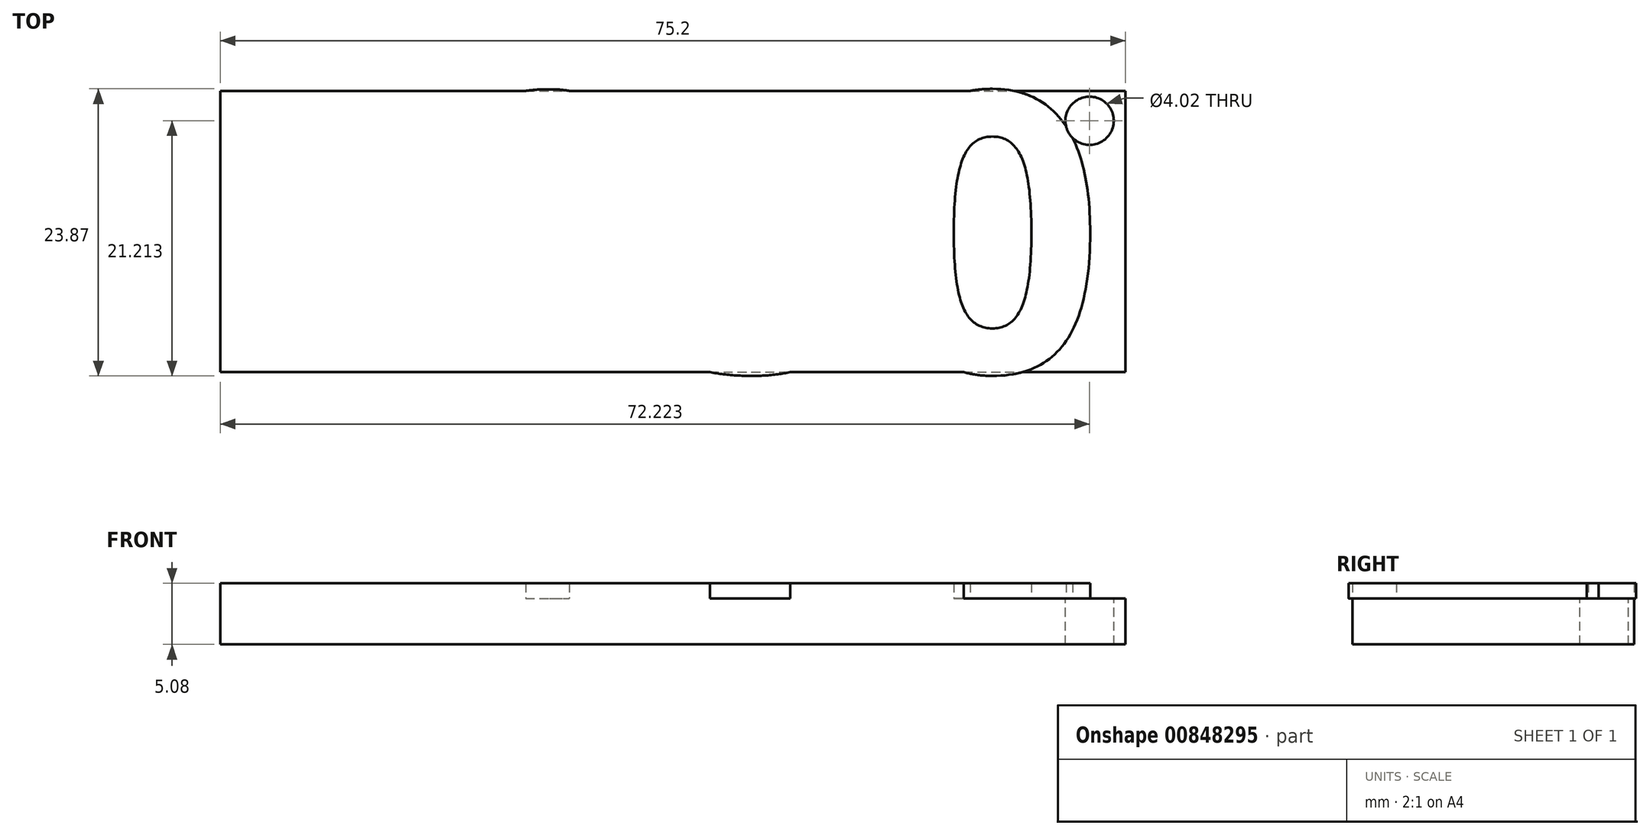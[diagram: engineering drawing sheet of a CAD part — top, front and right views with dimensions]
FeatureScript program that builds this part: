
annotation { "Feature Type Name" : "Feature", "Feature Type Description" : "" }
export const myFeature = defineFeature(function(context is Context, id is Id, definition is map)
    precondition{}
    {
        {
            var Q0;
            Q0=qCreatedBy(makeId("Top.planeOp"),FACE);
            var sketch = newSketch(context, id + "F0", { "sketchPlane" : qUnion([Q0])});
            skLineSegment(sketch, "E0.bottom", {"start": v(-35.42, 25.56) * mm, "end": v(39.78, 25.56) * mm});
            skLineSegment(sketch, "E0.top", {"start": v(-35.42, 2.18) * mm, "end": v(39.78, 2.18) * mm});
            skLineSegment(sketch, "E0.left", {"start": v(-35.42, 25.56) * mm, "end": v(-35.42, 2.18) * mm});
            skLineSegment(sketch, "E0.right", {"start": v(39.78, 25.56) * mm, "end": v(39.78, 2.18) * mm});
            skSolve(sketch);
        }
        {
            var Q0;
            Q0 = qSketchRegion(id + "F0", true);
            extrude(context, id + "F1", {"entities" : qUnion([Q0]), "depth" : 3.8 * mm, "offsetDistance" : 25.4 * mm});
        }
        {
            var Q0;
            Q0=makeQuery(id+"F1.opExtrude","CAP_FACE",FACE,{"disambiguationData":[OSD([sQuery(id+"F0.wireOp",EDGE,"E0.bottom"),sQuery(id+"F0.wireOp",EDGE,"E0.top"),sQuery(id+"F0.wireOp",EDGE,"E0.left"),sQuery(id+"F0.wireOp",EDGE,"E0.right")])],"isStart":false});
            var sketch = newSketch(context, id + "F2", { "sketchPlane" : qUnion([Q0])});
            skText(sketch, "E1", { "text": "F250", "fontName": "OpenSans-Bold.ttf"});
            const initialGuessF2  = {"E1": [-0.03542, 0.00218, 1, 0, 0.02338]};
            skSetInitialGuess(sketch, initialGuessF2);
            skSolve(sketch);
        }
        {
            var Q0;
            Q0=makeQuery(id+"F2.imprint","IMPRINT",FACE,{"disambiguationData":[TD([[makeQuery(id+"F2.imprint","IMPRINT",EDGE,{"derivedFrom":sQuery(id+"F2.wireOp",EDGE,"E1.sketch_text.stroke-0")}),1.0]])]});
            var Q1;
            Q1 = qSketchRegion(id + "F2", true);
            extrude(context, id + "F3", {"entities" : qUnion([Q0, Q1]), "operationType" : NewBodyOperationType.ADD, "depth" : 1.27 * mm, "offsetDistance" : 25.4 * mm});
        }
        {
            var Q0;
            Q0=makeQuery(id+"F3.opExtrude","CAP_FACE",FACE,{"disambiguationData":[OSD([sQuery(id+"F2.wireOp",EDGE,"E1.sketch_text.stroke-54"),sQuery(id+"F2.wireOp",EDGE,"E1.sketch_text.stroke-55"),sQuery(id+"F2.wireOp",EDGE,"E1.sketch_text.stroke-56"),sQuery(id+"F2.wireOp",EDGE,"E1.sketch_text.stroke-57"),sQuery(id+"F2.wireOp",EDGE,"E1.sketch_text.stroke-58"),sQuery(id+"F2.wireOp",EDGE,"E1.sketch_text.stroke-59"),sQuery(id+"F2.wireOp",EDGE,"E1.sketch_text.stroke-60"),sQuery(id+"F2.wireOp",EDGE,"E1.sketch_text.stroke-61"),sQuery(id+"F2.wireOp",EDGE,"E1.sketch_text.stroke-62"),sQuery(id+"F2.wireOp",EDGE,"E1.sketch_text.stroke-63"),sQuery(id+"F2.wireOp",EDGE,"E1.sketch_text.stroke-64"),sQuery(id+"F2.wireOp",EDGE,"E1.sketch_text.stroke-65"),sQuery(id+"F2.wireOp",EDGE,"E1.sketch_text.stroke-66"),sQuery(id+"F2.wireOp",EDGE,"E1.sketch_text.stroke-67"),sQuery(id+"F2.wireOp",EDGE,"E1.sketch_text.stroke-68"),sQuery(id+"F2.wireOp",EDGE,"E1.sketch_text.stroke-69")])],"isStart":false});
            var sketch = newSketch(context, id + "F4", { "sketchPlane" : qUnion([Q0])});
            skCircle(sketch, "E2", {"center": v(36.8, 23.07) * mm, "radius": 2 * mm});
            skSolve(sketch);
        }
        {
            var Q0;
            Q0 = qSketchRegion(id + "F4", true);
            extrude(context, id + "F5", {"entities" : qUnion([Q0]), "operationType" : NewBodyOperationType.REMOVE, "oppositeDirection" : true, "depth" : 20.12 * mm, "offsetDistance" : 25.4 * mm});
        }
    });
